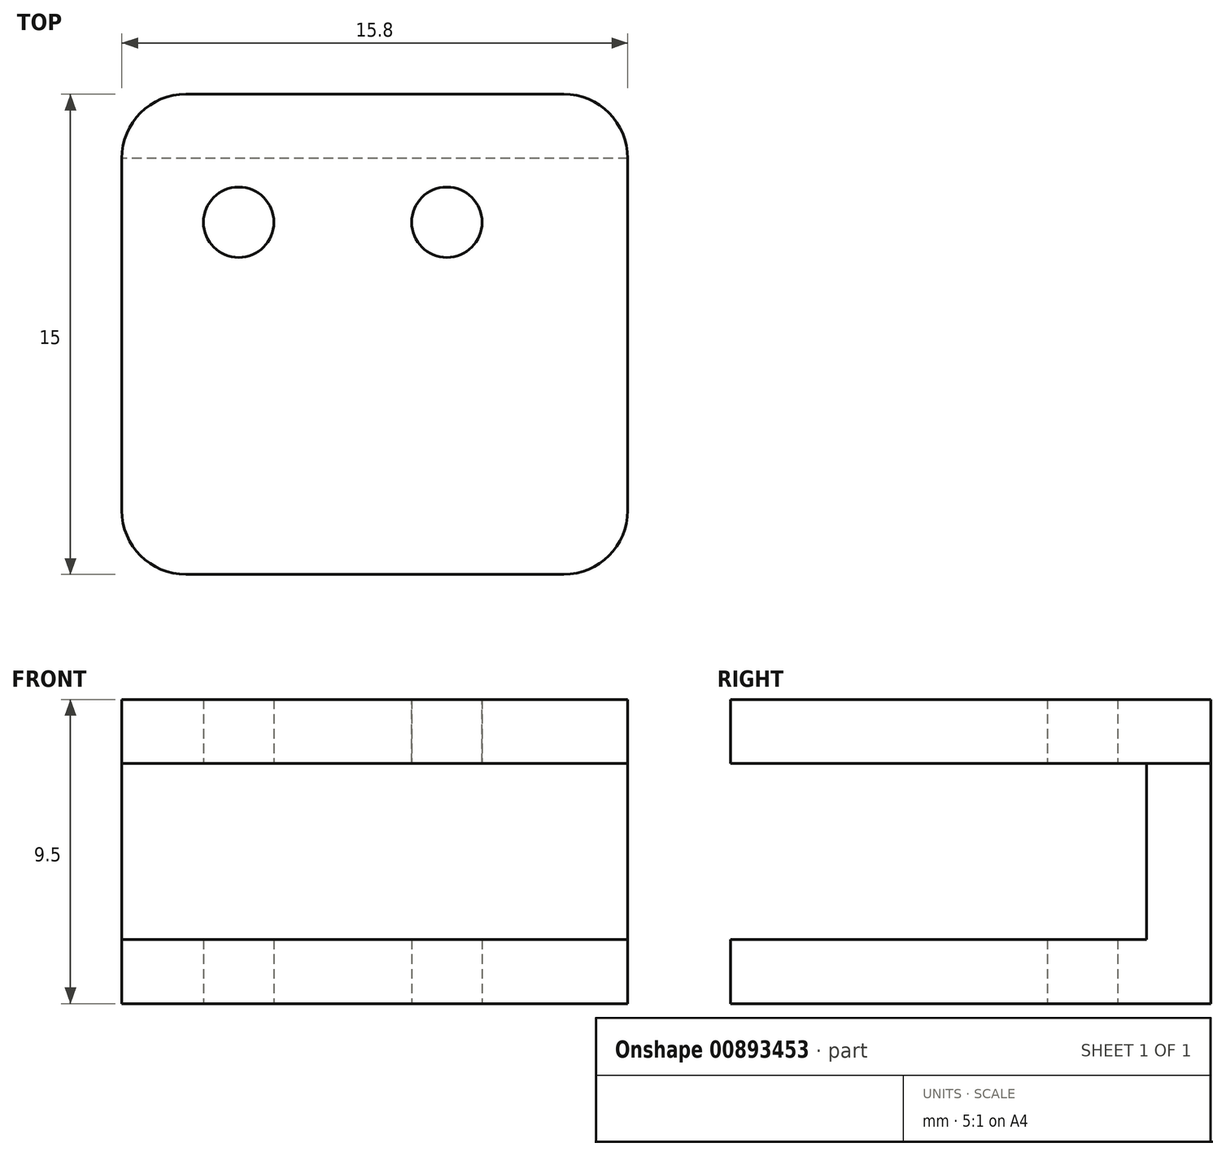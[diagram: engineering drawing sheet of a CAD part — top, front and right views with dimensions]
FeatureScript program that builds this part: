
annotation { "Feature Type Name" : "Feature", "Feature Type Description" : "" }
export const myFeature = defineFeature(function(context is Context, id is Id, definition is map)
    precondition{}
    {
        {
            var Q0;
            Q0=qCreatedBy(makeId("Top.planeOp"),FACE);
            var sketch = newSketch(context, id + "F0", { "sketchPlane" : qUnion([Q0])});
            skLineSegment(sketch, "E0.bottom", {"start": v(0, 23.83) * mm, "end": v(0, 23.83) * mm});
            skLineSegment(sketch, "E0.top", {"start": v(0, -23.13) * mm, "end": v(0, -23.13) * mm});
            skLineSegment(sketch, "E0.left", {"start": v(0, 23.83) * mm, "end": v(0, -23.13) * mm, "construction": true});
            skLineSegment(sketch, "E0.right", {"start": v(0, 23.83) * mm, "end": v(0, -23.13) * mm, "construction": true});
            skLineSegment(sketch, "E1", {"start": v(0, 3.4) * mm, "end": v(-7.9, 3.4) * mm});
            skLineSegment(sketch, "E2", {"start": v(-7.9, 3.4) * mm, "end": v(-7.9, -11.6) * mm});
            skLineSegment(sketch, "E3", {"start": v(-7.9, -11.6) * mm, "end": v(0, -11.6) * mm});
            skLineSegment(sketch, "E4.MirrorCS", {"start": v(0, 3.4) * mm, "end": v(7.9, 3.4) * mm});
            skLineSegment(sketch, "E5.MirrorCS", {"start": v(7.9, 3.4) * mm, "end": v(7.9, -11.6) * mm});
            skLineSegment(sketch, "E6.MirrorCS", {"start": v(7.9, -11.6) * mm, "end": v(0, -11.6) * mm});
            skCircle(sketch, "E7", {"center": v(-4.25, -0.6) * mm, "radius": 1.1 * mm});
            skCircle(sketch, "E8.MirrorC", {"center": v(2.25, -0.6) * mm, "radius": 1.1 * mm});
            skSolve(sketch);
        }
        {
            var Q0;
            Q0=makeQuery(id+"F0.imprint","IMPRINT",FACE,{"disambiguationData":[TD([[makeQuery(id+"F0.imprint","IMPRINT",EDGE,{"derivedFrom":sQuery(id+"F0.wireOp",EDGE,"E1")}),1.0]])]});
            extrude(context, id + "F1", {"entities" : qUnion([Q0]), "offsetDistance" : 25 * mm, "depth" : 9.5 * mm});
        }
        {
            var Q0;
            Q0=makeQuery(id+"F1.opExtrude","SWEPT_EDGE",EDGE,{"disambiguationData":[OSD([sQuery(id+"F0.wireOp",EDGE,"E5.MirrorCS"),sQuery(id+"F0.wireOp",EDGE,"E6.MirrorCS")])]});
            var Q1;
            Q1=makeQuery(id+"F1.opExtrude","SWEPT_EDGE",EDGE,{"disambiguationData":[OSD([sQuery(id+"F0.wireOp",EDGE,"E4.MirrorCS"),sQuery(id+"F0.wireOp",EDGE,"E5.MirrorCS")])]});
            var Q2;
            Q2=makeQuery(id+"F1.opExtrude","SWEPT_EDGE",EDGE,{"disambiguationData":[OSD([sQuery(id+"F0.wireOp",EDGE,"E2"),sQuery(id+"F0.wireOp",EDGE,"E3")])]});
            var Q3;
            Q3=makeQuery(id+"F1.opExtrude","SWEPT_EDGE",EDGE,{"disambiguationData":[OSD([sQuery(id+"F0.wireOp",EDGE,"E1"),sQuery(id+"F0.wireOp",EDGE,"E2")])]});
            fillet(context, id + "F2", {"entities" : qUnion([Q0, Q1, Q2, Q3]), "radius" : 2 * mm, "tangentPropagation" : true, "allowEdgeOverflow" : false});
        }
        {
            var Q0;
            Q0=makeQuery(id+"F1.opExtrude","SWEPT_FACE",FACE,{"disambiguationData":[OSD([sQuery(id+"F0.wireOp",EDGE,"E2")])]});
            var sketch = newSketch(context, id + "F3", { "sketchPlane" : qUnion([Q0])});
            skLineSegment(sketch, "E9.bottom", {"start": v(-1.4, 2) * mm, "end": v(21.5, 2) * mm});
            skLineSegment(sketch, "E9.top", {"start": v(-1.4, 7.5) * mm, "end": v(21.5, 7.5) * mm});
            skLineSegment(sketch, "E9.left", {"start": v(-1.4, 2) * mm, "end": v(-1.4, 7.5) * mm});
            skLineSegment(sketch, "E9.right", {"start": v(21.5, 2) * mm, "end": v(21.5, 7.5) * mm});
            skSolve(sketch);
        }
        {
            var Q0;
            {var subQ0=sQuery(id+"F3.wireOp",EDGE,"E9.left");Q0=makeQuery(id+"F3.imprint","IMPRINT",FACE,{"disambiguationData":[TD([[makeQuery(id+"F3.imprint","IMPRINT",EDGE,{"derivedFrom":subQ0}),1.0]])]});}
            var Q1;
            {var subQ0=sQuery(id+"F3.wireOp",EDGE,"E9.right");Q1=makeQuery(id+"F3.imprint","IMPRINT",FACE,{"disambiguationData":[TD([[makeQuery(id+"F3.imprint","IMPRINT",EDGE,{"derivedFrom":subQ0}),1.0]])]});}
            extrude(context, id + "F4", {"entities" : qUnion([Q0, Q1]), "operationType" : NewBodyOperationType.REMOVE, "oppositeDirection" : true, "depth" : 25 * mm, "offsetDistance" : 25 * mm});
        }
        {
            var Q0;
            Q0=makeQuery(id+"F1.opExtrude","CAP_FACE",FACE,{"disambiguationData":[OSD([sQuery(id+"F0.wireOp",EDGE,"E1"),sQuery(id+"F0.wireOp",EDGE,"E2"),sQuery(id+"F0.wireOp",EDGE,"E3"),sQuery(id+"F0.wireOp",EDGE,"E4.MirrorCS"),sQuery(id+"F0.wireOp",EDGE,"E5.MirrorCS"),sQuery(id+"F0.wireOp",EDGE,"E6.MirrorCS"),sQuery(id+"F0.wireOp",EDGE,"E7"),sQuery(id+"F0.wireOp",EDGE,"E8.MirrorC")])],"isStart":false});
            var sketch = newSketch(context, id + "F5", { "sketchPlane" : qUnion([Q0])});
            skCircle(sketch, "E10", {"center": v(2.25, -0.6) * mm, "radius": 1.1 * mm});
            skCircle(sketch, "E11", {"center": v(-4.25, -0.6) * mm, "radius": 1.1 * mm});
            skSolve(sketch);
        }
        {
            var Q0;
            Q0=makeQuery(id+"F5.imprint","IMPRINT",FACE,{"disambiguationData":[TD([[makeQuery(id+"F5.imprint","IMPRINT",EDGE,{"derivedFrom":sQuery(id+"F5.wireOp",EDGE,"E11")}),1.0]])]});
            var Q1;
            Q1=makeQuery(id+"F5.imprint","IMPRINT",FACE,{"disambiguationData":[TD([[makeQuery(id+"F5.imprint","IMPRINT",EDGE,{"derivedFrom":sQuery(id+"F5.wireOp",EDGE,"E10")}),-1.0]])]});
            extrude(context, id + "F6", {"entities" : qUnion([Q0, Q1]), "oppositeDirection" : true, "depth" : 2 * mm, "offsetDistance" : 25 * mm});
        }
    });
